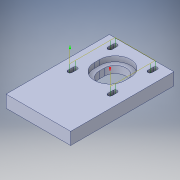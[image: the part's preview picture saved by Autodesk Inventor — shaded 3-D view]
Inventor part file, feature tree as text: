
AUTODESK INVENTOR PART (.ipt)
format: ipt  version: 2016 (Build 200138000, 138)  size: 248,320 bytes
history: native  units: in
note: dims shown in document units (in); Inventor stores cm internally (conversion verified against a paired STEP export)
features: sketch x1, other x1
ambient origin geometry x8: Origin, YZ Plane, XZ Plane, XY Plane, X Axis, Y Axis, Z Axis, Center Point
bodies: Solid1 (feature_tree)
feature tree (2):
  sketch  "Sketch1"
  other  "Cut-Extrude2"
